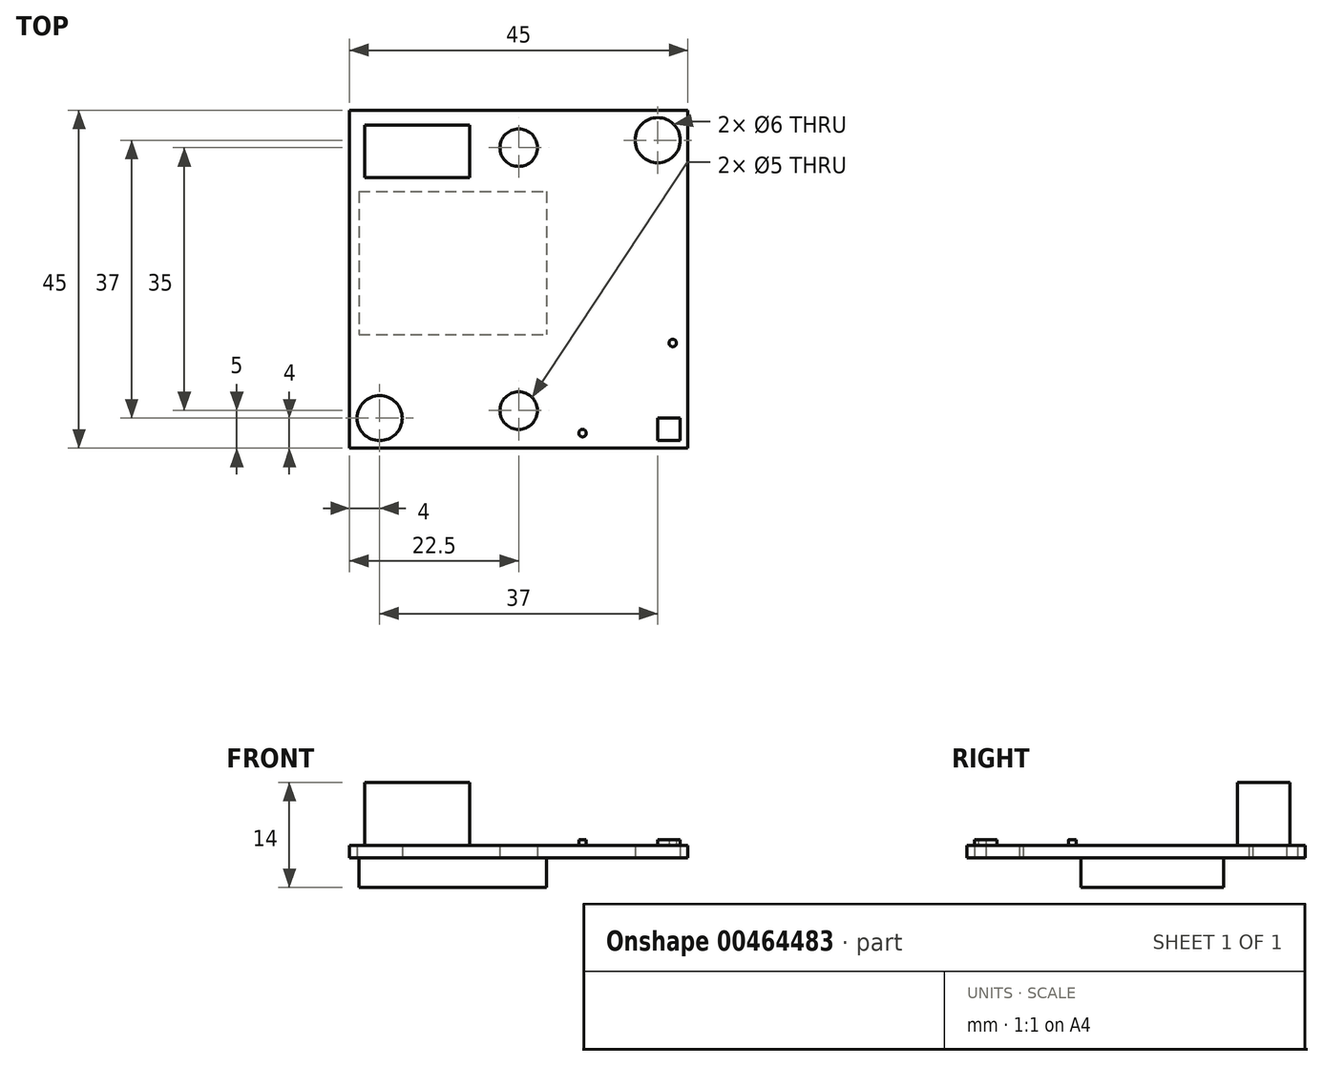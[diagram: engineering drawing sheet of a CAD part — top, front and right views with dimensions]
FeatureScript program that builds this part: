
annotation { "Feature Type Name" : "Feature", "Feature Type Description" : "" }
export const myFeature = defineFeature(function(context is Context, id is Id, definition is map)
    precondition{}
    {
        {
            var Q0;
            Q0=qCreatedBy(makeId("Top.planeOp"),FACE);
            var sketch = newSketch(context, id + "F0", { "sketchPlane" : qUnion([Q0])});
            skLineSegment(sketch, "E0.bottom", {"start": v(22.5, 22.5) * mm, "end": v(-22.5, 22.5) * mm});
            skLineSegment(sketch, "E0.top", {"start": v(22.5, -22.5) * mm, "end": v(-22.5, -22.5) * mm});
            skLineSegment(sketch, "E0.left", {"start": v(22.5, 22.5) * mm, "end": v(22.5, -22.5) * mm});
            skLineSegment(sketch, "E0.right", {"start": v(-22.5, 22.5) * mm, "end": v(-22.5, -22.5) * mm});
            skPoint(sketch, "E0.middle", {"position": v(0, 0) * mm});
            skCircle(sketch, "E1", {"center": v(0, 17.5) * mm, "radius": 2.5 * mm});
            skLineSegment(sketch, "E2", {"start": v(-22.5, 0) * mm, "end": v(22.5, 0) * mm, "construction": true});
            skCircle(sketch, "E3.MirrorC", {"center": v(0, -17.5) * mm, "radius": 2.5 * mm});
            skCircle(sketch, "E4", {"center": v(18.5, 18.5) * mm, "radius": 3 * mm});
            skLineSegment(sketch, "E5", {"start": v(0, 0) * mm, "end": v(22.5, 22.5) * mm, "construction": true});
            skLineSegment(sketch, "E6", {"start": v(-22.5, 22.5) * mm, "end": v(22.5, -22.5) * mm, "construction": true});
            skCircle(sketch, "E7.MirrorC", {"center": v(-18.5, -18.5) * mm, "radius": 3 * mm});
            skSolve(sketch);
        }
        {
            var Q0;
            Q0=makeQuery(id+"F0.imprint","IMPRINT",FACE,{"disambiguationData":[TD([[makeQuery(id+"F0.imprint","IMPRINT",EDGE,{"derivedFrom":sQuery(id+"F0.wireOp",EDGE,"E0.bottom")}),1.0]])]});
            extrude(context, id + "F1", {"entities" : qUnion([Q0]), "depth" : 1.6 * mm});
        }
        {
            var Q0;
            Q0=makeQuery(id+"F1.opExtrude","CAP_FACE",FACE,{"disambiguationData":[OSD([sQuery(id+"F0.wireOp",EDGE,"E0.bottom"),sQuery(id+"F0.wireOp",EDGE,"E0.top"),sQuery(id+"F0.wireOp",EDGE,"E0.left"),sQuery(id+"F0.wireOp",EDGE,"E0.right"),sQuery(id+"F0.wireOp",EDGE,"E1"),sQuery(id+"F0.wireOp",EDGE,"E3.MirrorC"),sQuery(id+"F0.wireOp",EDGE,"E4"),sQuery(id+"F0.wireOp",EDGE,"E7.MirrorC")])],"isStart":false});
            var sketch = newSketch(context, id + "F2", { "sketchPlane" : qUnion([Q0])});
            skLineSegment(sketch, "E8.bottom", {"start": v(18.5, -18.5) * mm, "end": v(21.5, -18.5) * mm});
            skLineSegment(sketch, "E8.top", {"start": v(18.5, -21.5) * mm, "end": v(21.5, -21.5) * mm});
            skLineSegment(sketch, "E8.left", {"start": v(18.5, -18.5) * mm, "end": v(18.5, -21.5) * mm});
            skLineSegment(sketch, "E8.right", {"start": v(21.5, -18.5) * mm, "end": v(21.5, -21.5) * mm});
            skCircle(sketch, "E9", {"center": v(20.5, -8.5) * mm, "radius": 0.5 * mm});
            skCircle(sketch, "E10", {"center": v(8.5, -20.5) * mm, "radius": 0.5 * mm});
            skSolve(sketch);
        }
        {
            var Q0;
            Q0 = qSketchRegion(id + "F2", true);
            extrude(context, id + "F3", {"entities" : qUnion([Q0]), "operationType" : NewBodyOperationType.ADD, "depth" : .75 * mm});
        }
        {
            var Q0;
            Q0=makeQuery(id+"F1.opExtrude","CAP_FACE",FACE,{"disambiguationData":[OSD([sQuery(id+"F0.wireOp",EDGE,"E0.bottom"),sQuery(id+"F0.wireOp",EDGE,"E0.top"),sQuery(id+"F0.wireOp",EDGE,"E0.left"),sQuery(id+"F0.wireOp",EDGE,"E0.right"),sQuery(id+"F0.wireOp",EDGE,"E1"),sQuery(id+"F0.wireOp",EDGE,"E3.MirrorC"),sQuery(id+"F0.wireOp",EDGE,"E4"),sQuery(id+"F0.wireOp",EDGE,"E7.MirrorC")])],"isStart":true});
            var sketch = newSketch(context, id + "F4", { "sketchPlane" : qUnion([Q0])});
            skLineSegment(sketch, "E11.bottom", {"start": v(-21.27, -11.65) * mm, "end": v(3.73, -11.65) * mm});
            skLineSegment(sketch, "E11.top", {"start": v(-21.27, 7.35) * mm, "end": v(3.73, 7.35) * mm});
            skLineSegment(sketch, "E11.left", {"start": v(-21.27, -11.65) * mm, "end": v(-21.27, 7.35) * mm});
            skLineSegment(sketch, "E11.right", {"start": v(3.73, -11.65) * mm, "end": v(3.73, 7.35) * mm});
            skSolve(sketch);
        }
        {
            var Q0;
            Q0 = qSketchRegion(id + "F4", true);
            extrude(context, id + "F5", {"entities" : qUnion([Q0]), "operationType" : NewBodyOperationType.ADD, "depth" : 4 * mm});
        }
        {
            var Q0;
            Q0=makeQuery(id+"F1.opExtrude","CAP_FACE",FACE,{"disambiguationData":[OSD([sQuery(id+"F0.wireOp",EDGE,"E0.bottom"),sQuery(id+"F0.wireOp",EDGE,"E0.top"),sQuery(id+"F0.wireOp",EDGE,"E0.left"),sQuery(id+"F0.wireOp",EDGE,"E0.right"),sQuery(id+"F0.wireOp",EDGE,"E1"),sQuery(id+"F0.wireOp",EDGE,"E3.MirrorC"),sQuery(id+"F0.wireOp",EDGE,"E4"),sQuery(id+"F0.wireOp",EDGE,"E7.MirrorC")])],"isStart":false});
            var sketch = newSketch(context, id + "F6", { "sketchPlane" : qUnion([Q0])});
            skLineSegment(sketch, "E12.bottom", {"start": v(-20.5, 20.5) * mm, "end": v(-6.5, 20.5) * mm});
            skLineSegment(sketch, "E12.top", {"start": v(-20.5, 13.5) * mm, "end": v(-6.5, 13.5) * mm});
            skLineSegment(sketch, "E12.right", {"start": v(-6.5, 20.5) * mm, "end": v(-6.5, 13.5) * mm});
            skLineSegment(sketch, "E13", {"start": v(-20.5, 20.5) * mm, "end": v(-20.5, 13.5) * mm});
            skSolve(sketch);
        }
        {
            var Q0;
            Q0 = qSketchRegion(id + "F6", true);
            extrude(context, id + "F7", {"entities" : qUnion([Q0]), "operationType" : NewBodyOperationType.ADD, "depth" : 8.4 * mm});
        }
    });
